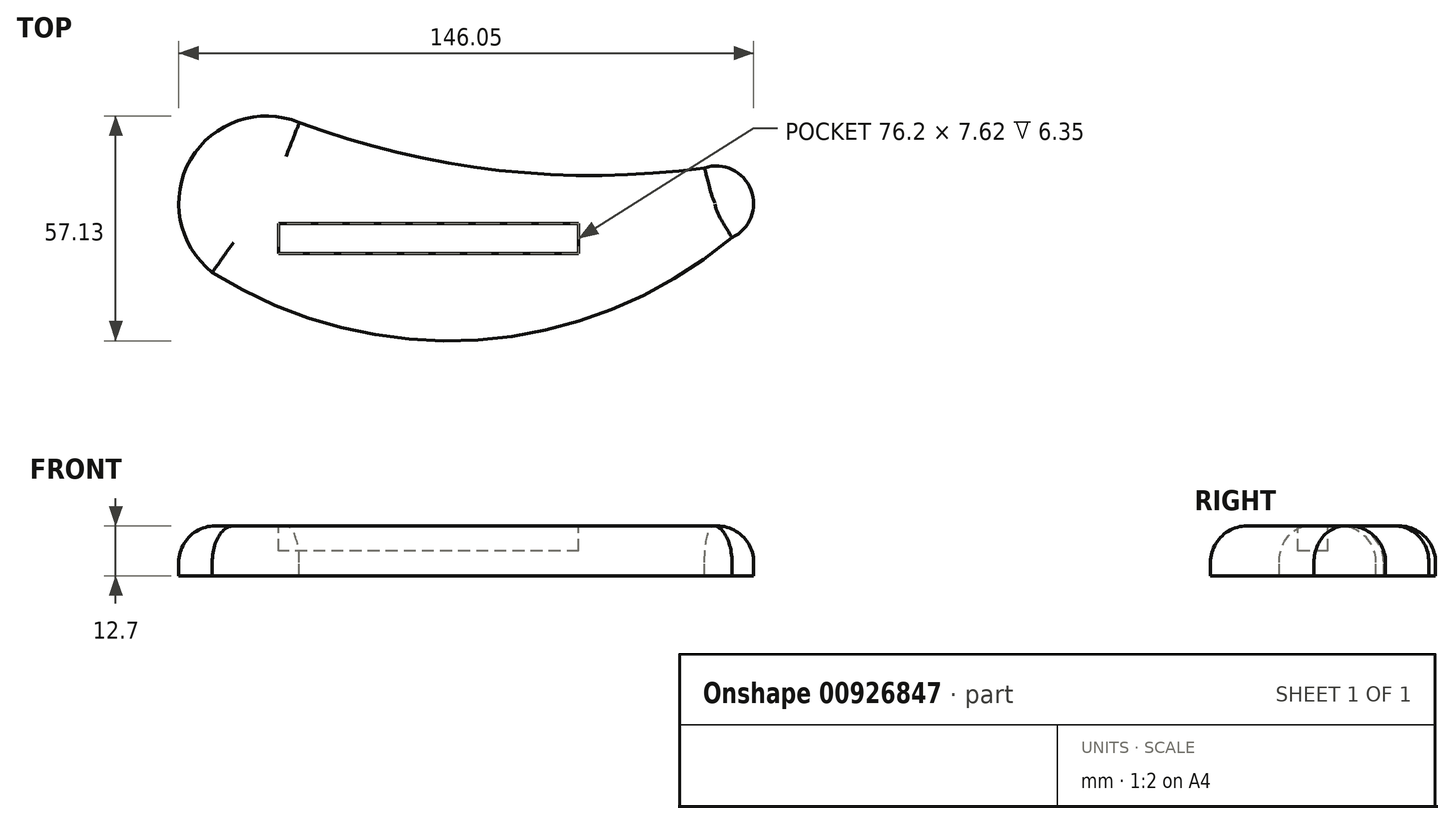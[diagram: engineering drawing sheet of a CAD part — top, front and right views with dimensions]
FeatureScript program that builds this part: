
annotation { "Feature Type Name" : "Feature", "Feature Type Description" : "" }
export const myFeature = defineFeature(function(context is Context, id is Id, definition is map)
    precondition{}
    {
        {
            var Q0;
            Q0=qCreatedBy(makeId("Top.planeOp"),FACE);
            var sketch = newSketch(context, id + "F0", { "sketchPlane" : qUnion([Q0])});
            skLineSegment(sketch, "E0", {"start": v(0, 0) * mm, "end": v(0, 28.93) * mm, "construction": true});
            skLineSegment(sketch, "E1", {"start": v(0, 0) * mm, "end": v(32.03, 0) * mm, "construction": true});
            skSolve(sketch);
        }
        {
            var Q0;
            Q0=qCreatedBy(makeId("Top.planeOp"),FACE);
            var sketch = newSketch(context, id + "F1", { "sketchPlane" : qUnion([Q0])});
            skArc(sketch, "E2", {"start": v(30.63, 42.8) * mm, "mid": v(3.01, 33.4) * mm, "end": v(8.5, 4.74) * mm});
            skArc(sketch, "E3", {"start": v(140.55, 13.6) * mm, "mid": v(145.4, 25.7) * mm, "end": v(133.6, 31.29) * mm});
            skLineSegment(sketch, "E4", {"start": v(22.23, 22.23) * mm, "end": v(136.53, 22.23) * mm, "construction": true});
            skArc(sketch, "E5", {"start": v(30.63, 42.8) * mm, "mid": v(81.4, 30.66) * mm, "end": v(133.6, 31.29) * mm});
            skArc(sketch, "E6", {"start": v(8.5, 4.74) * mm, "mid": v(75.97, -12.42) * mm, "end": v(140.55, 13.6) * mm});
            skSolve(sketch);
        }
        {
            var Q0;
            Q0=makeQuery(id+"F1.imprint","IMPRINT",FACE,{"disambiguationData":[TD([[makeQuery(id+"F1.imprint","IMPRINT",EDGE,{"derivedFrom":sQuery(id+"F1.wireOp",EDGE,"E2")}),1.0]])]});
            extrude(context, id + "F2", {"entities" : qUnion([Q0]), "oppositeDirection" : true, "depth" : 12.7 * mm, "offsetDistance" : 25.4 * mm});
        }
        {
            var Q0;
            Q0=makeQuery(id+"F2.opExtrude","CAP_EDGE",EDGE,{"disambiguationData":[OSD([sQuery(id+"F1.wireOp",EDGE,"E2")])],"isStart":true});
            var Q1;
            Q1=makeQuery(id+"F2.opExtrude","CAP_EDGE",EDGE,{"disambiguationData":[OSD([sQuery(id+"F1.wireOp",EDGE,"E5")])],"isStart":true});
            var Q2;
            Q2=makeQuery(id+"F2.opExtrude","CAP_EDGE",EDGE,{"disambiguationData":[OSD([sQuery(id+"F1.wireOp",EDGE,"E6")])],"isStart":true});
            var Q3;
            Q3=makeQuery(id+"F2.opExtrude","CAP_EDGE",EDGE,{"disambiguationData":[OSD([sQuery(id+"F1.wireOp",EDGE,"E3")])],"isStart":true});
            fillet(context, id + "F3", {"entities" : qUnion([Q0, Q1, Q2, Q3]), "radius" : 9.27 * mm, "tangentPropagation" : true, "allowEdgeOverflow" : false});
        }
        {
            var Q0;
            Q0=qCreatedBy(makeId("Top.planeOp"),FACE);
            var sketch = newSketch(context, id + "F4", { "sketchPlane" : qUnion([Q0])});
            skLineSegment(sketch, "E7", {"start": v(25.4, 17.14) * mm, "end": v(25.4, 9.53) * mm});
            skLineSegment(sketch, "E8", {"start": v(25.4, 9.52) * mm, "end": v(101.6, 9.53) * mm});
            skLineSegment(sketch, "E9", {"start": v(101.6, 9.53) * mm, "end": v(101.6, 17.15) * mm});
            skLineSegment(sketch, "E10", {"start": v(101.6, 17.15) * mm, "end": v(25.4, 17.14) * mm});
            skSolve(sketch);
        }
        {
            var Q0;
            Q0 = qSketchRegion(id + "F4", true);
            extrude(context, id + "F5", {"entities" : qUnion([Q0]), "operationType" : NewBodyOperationType.REMOVE, "oppositeDirection" : true, "depth" : 6.35 * mm, "offsetDistance" : 25.4 * mm});
        }
    });
